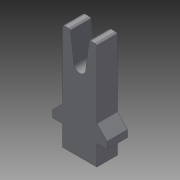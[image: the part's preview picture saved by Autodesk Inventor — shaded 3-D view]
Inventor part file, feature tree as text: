
AUTODESK INVENTOR PART (.ipt)
format: ipt  version: 2015 (Build 190159000, 159)  size: 129,024 bytes
history: native  units: in
note: dims shown in document units (in); Inventor stores cm internally (conversion verified against a paired STEP export)
features: extrude x3, sketch x3, reference x3, chamfer x1, fillet x1, projected_geometry x1
ambient origin geometry x8: Origin, YZ Plane, XZ Plane, XY Plane, X Axis, Y Axis, Z Axis, Center Point
bodies: Solid1 (feature_tree)
feature tree (12):
  extrude  "Extrusion1"  Depth=0.6299in
  extrude  "Extrusion2"  Depth=1.2205in
  chamfer  "Chamfer1"  Distance=0.2362in
  extrude  "Extrusion3"  Depth=0.3937in
  fillet  "Fillet1"  Radius=0.0886in
  sketch  "Sketch1"  dims[d0=0.6299in d2=0.0787in]
  reference  "Reference1"
  reference  "Reference2"
  reference  "Reference3"
  sketch  "Sketch2"  dims[d3=0.2362in d4=0.0in d6=1.2205in d7=0.2362in d8=0.0in]
  sketch  "Sketch3"  dims[d9=0.1181in d10=0.125in d11=45.0deg d12=0.0886in d13=0.0886in d14=0.315in d17=0.1378in d18=0.2362in d19=0.0in d20=0.0197in d21=0.3937in]
  projected_geometry  "Projected Loop1"
